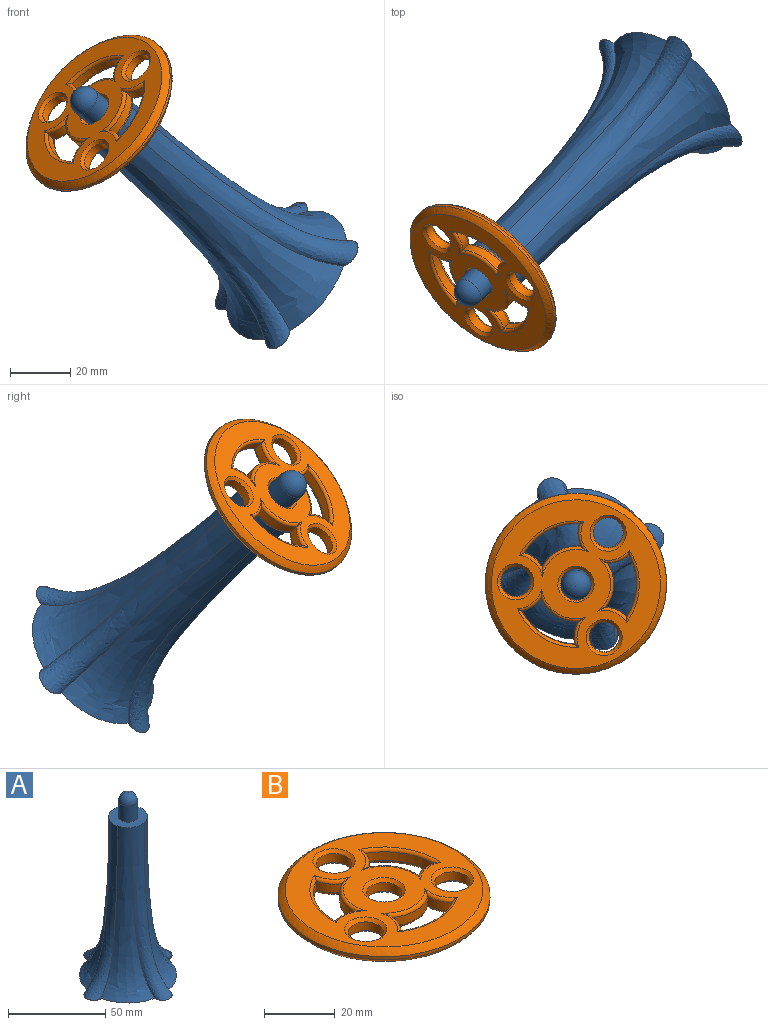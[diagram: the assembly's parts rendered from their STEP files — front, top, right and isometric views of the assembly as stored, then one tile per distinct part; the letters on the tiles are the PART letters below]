
ASSEMBLY  parts=2 mates=1
PART A: 12 faces, bbox 60x60x115 mm
  f0: plane 60x60mm, normal (0,0,-1), area 2127.2mm2, adj f2,f3,f4,f5,f6,f7,f8,f9
  f1: plane 20x20mm, normal (0,0,1), area 235.6mm2, adj f2,f3,f4,f5,f6,f7,f8,f9
  f2: bspline ~100x22.51mm, area 1248.8mm2, adj f0,f1,f3,f9
  f3: bspline ~100x21.66mm, area 955.2mm2, adj f0,f1,f2,f4
  f4: bspline ~100x22.51mm, area 1248.8mm2, adj f0,f1,f3,f5
  f5: bspline ~100x21.66mm, area 955.2mm2, adj f0,f1,f4,f6
  f6: bspline ~100x22.51mm, area 1248.8mm2, adj f0,f1,f5,f7
  f7: bspline ~100x21.66mm, area 955.2mm2, adj f0,f1,f6,f8
  f8: bspline ~100x22.51mm, area 1248.8mm2, adj f0,f1,f7,f9
  f9: bspline ~100x21.66mm, area 955.2mm2, adj f0,f1,f2,f8
  f10: cylinder r=5mm len=10mm, axis (0,0,-1), area 314.2mm2, adj f1,f11
  f11: sphere r=5mm, area 157.1mm2, adj f10
PART B: 53 faces, bbox 60x60x5 mm
  f0: cylinder r=20mm len=17.86mm, axis (0,0,-1), area 65mm2, adj f1,f12,f29,f48
  f1: cylinder r=10mm len=7.56mm, axis (0,0,-1), area 23.4mm2, adj f0,f2,f30,f46
  f2: cylinder r=12.5mm len=12.68mm, axis (0,0,-1), area 46.9mm2, adj f1,f12,f32,f45
  f3: cylinder r=20mm len=20.63mm, axis (0,0,-1), area 65mm2, adj f4,f13,f33,f44
  f4: cylinder r=10mm len=7mm, axis (0,0,-1), area 23.4mm2, adj f3,f5,f34,f42
  f5: cylinder r=12.5mm len=14.64mm, axis (0,0,-1), area 46.9mm2, adj f4,f13,f36,f41
  f6: cylinder r=20mm len=17.86mm, axis (0,0,-1), area 65mm2, adj f7,f15,f37,f49
  f7: cylinder r=10mm len=6.09mm, axis (0,0,-1), area 23.4mm2, adj f6,f8,f38,f50
  f8: cylinder r=12.5mm len=12.68mm, axis (0,0,-1), area 46.9mm2, adj f7,f15,f40,f52
  f9: cylinder r=5mm len=10mm, axis (0,0,-1), area 94.2mm2, adj f22,f26
  f10: cylinder r=5mm len=10mm, axis (0,0,-1), area 94.2mm2, adj f24,f28
  f11: cylinder r=5mm len=10mm, axis (0,0,-1), area 94.2mm2, adj f23,f27
  f12: cylinder r=10mm len=6.09mm, axis (0,0,-1), area 23.4mm2, adj f0,f2,f31,f47
  f13: cylinder r=10mm len=7mm, axis (0,0,-1), area 23.4mm2, adj f3,f5,f35,f43
  f14: cylinder r=30mm len=60mm, axis (0,0,-1), area 188.5mm2, adj f19,f20
  f15: cylinder r=10mm len=7.56mm, axis (0,0,-1), area 23.4mm2, adj f6,f8,f39,f51
  f16: cylinder r=5mm len=10mm, axis (0,0,-1), area 94.2mm2, adj f21,f25
  f17: plane 56.01x56.01mm, normal (0,0,1), area 1435.9mm2, adj f19,f25,f26,f27,f28,f41,f42,f43
  f18: plane 56.01x56.01mm, normal (0,0,-1), area 1435.9mm2, adj f20,f21,f22,f23,f24,f29,f30,f31
  f19: bspline ~60x60mm, area 522.5mm2, adj f14,f17
  f20: bspline ~60x60mm, area 522.5mm2, adj f14,f18
  f21: cone r=6mm half-angle=45deg, axis (0,0,-1), area 48.9mm2, adj f16,f18
  f22: cone r=6mm half-angle=45deg, axis (0,0,-1), area 48.9mm2, adj f9,f18
  f23: cone r=6mm half-angle=45deg, axis (0,0,-1), area 48.9mm2, adj f11,f18
  f24: cone r=6mm half-angle=45deg, axis (0,0,-1), area 48.9mm2, adj f10,f18
  f25: cone r=5mm half-angle=45deg, axis (0,0,1), area 48.9mm2, adj f16,f17
  f26: cone r=5mm half-angle=45deg, axis (0,0,1), area 48.9mm2, adj f9,f17
  f27: cone r=5mm half-angle=45deg, axis (0,0,1), area 48.9mm2, adj f11,f17
  f28: cone r=5mm half-angle=45deg, axis (0,0,1), area 48.9mm2, adj f10,f17
  f29: torus R=21mm, axis (0,0,1), area 36.8mm2, adj f0,f18,f30,f31
  f30: torus R=9mm, axis (0,0,1), area 15mm2, adj f1,f18,f29,f32
  f31: torus R=9mm, axis (0,0,1), area 15mm2, adj f12,f18,f29,f32
  f32: torus R=11.5mm, axis (0,0,1), area 28.1mm2, adj f2,f18,f30,f31
  f33: torus R=21mm, axis (0,0,1), area 36.8mm2, adj f3,f18,f34,f35
  f34: torus R=9mm, axis (0,0,1), area 15mm2, adj f4,f18,f33,f36
  f35: torus R=9mm, axis (0,0,1), area 15mm2, adj f13,f18,f33,f36
  f36: torus R=11.5mm, axis (0,0,1), area 28.1mm2, adj f5,f18,f34,f35
  f37: torus R=21mm, axis (0,0,1), area 36.8mm2, adj f6,f18,f38,f39
  f38: torus R=9mm, axis (0,0,1), area 15mm2, adj f7,f18,f37,f40
  f39: torus R=9mm, axis (0,0,1), area 15mm2, adj f15,f18,f37,f40
  f40: torus R=11.5mm, axis (0,0,1), area 28.1mm2, adj f8,f18,f38,f39
  f41: torus R=11.5mm, axis (0,0,1), area 28.1mm2, adj f5,f17,f42,f43
  f42: torus R=9mm, axis (0,0,1), area 15mm2, adj f4,f17,f41,f44
  f43: torus R=9mm, axis (0,0,1), area 15mm2, adj f13,f17,f41,f44
  f44: torus R=21mm, axis (0,0,1), area 36.8mm2, adj f3,f17,f42,f43
  f45: torus R=11.5mm, axis (0,0,1), area 28.1mm2, adj f2,f17,f46,f47
  f46: torus R=9mm, axis (0,0,1), area 15mm2, adj f1,f17,f45,f48
  f47: torus R=9mm, axis (0,0,1), area 15mm2, adj f12,f17,f45,f48
  f48: torus R=21mm, axis (0,0,1), area 36.8mm2, adj f0,f17,f46,f47
  f49: torus R=21mm, axis (0,0,1), area 36.8mm2, adj f6,f17,f50,f51
  f50: torus R=9mm, axis (0,0,1), area 15mm2, adj f7,f17,f49,f52
  f51: torus R=9mm, axis (0,0,1), area 15mm2, adj f15,f17,f49,f52
  f52: torus R=11.5mm, axis (0,0,1), area 28.1mm2, adj f8,f17,f50,f51
PLACE A rot(axis=(0.54,0.12,-0.83),124.6deg) t=(114.92,42.19,-55.05)mm
PLACE B rot(axis=(0.33,-0.77,0.55),71.2deg) t=(54.3,-17.64,-2.65)mm
MATE revolute A.f10 <-> B.f14  axis (-0.61,-0.6,0.52) through (54.3,-17.64,-2.65)mm
